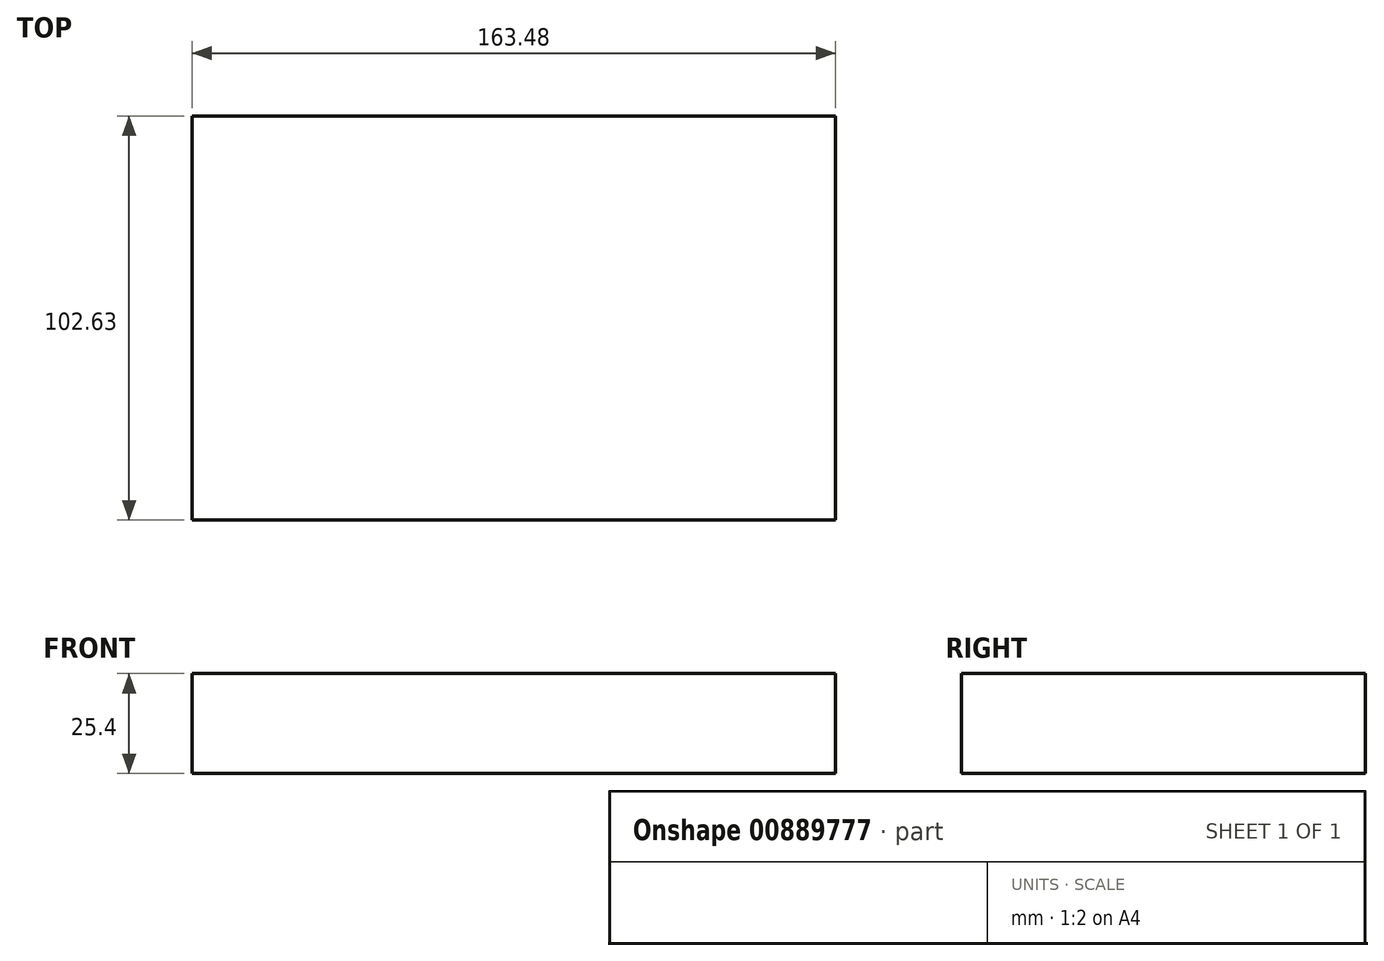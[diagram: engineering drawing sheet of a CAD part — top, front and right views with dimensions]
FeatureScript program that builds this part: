
annotation { "Feature Type Name" : "Feature", "Feature Type Description" : "" }
export const myFeature = defineFeature(function(context is Context, id is Id, definition is map)
    precondition{}
    {
        {
            var Q0;
            Q0=qCreatedBy(makeId("Top.planeOp"),FACE);
            var sketch = newSketch(context, id + "F0", { "sketchPlane" : qUnion([Q0])});
            skLineSegment(sketch, "E0.bottom", {"start": v(0, 0) * mm, "end": v(163.48, 0) * mm});
            skLineSegment(sketch, "E0.top", {"start": v(0, 102.63) * mm, "end": v(163.48, 102.63) * mm});
            skLineSegment(sketch, "E0.left", {"start": v(0, 0) * mm, "end": v(0, 102.63) * mm});
            skLineSegment(sketch, "E0.right", {"start": v(163.48, 0) * mm, "end": v(163.48, 102.63) * mm});
            skSolve(sketch);
        }
        {
            var Q0;
            Q0=makeQuery(id+"F0.imprint","IMPRINT",FACE,{"disambiguationData":[TD([[makeQuery(id+"F0.imprint","IMPRINT",EDGE,{"derivedFrom":sQuery(id+"F0.wireOp",EDGE,"E0.bottom")}),1.0]])]});
            extrude(context, id + "F1", {"entities" : qUnion([Q0]), "depth" : 25.4 * mm, "offsetDistance" : 25.4 * mm});
        }
    });
